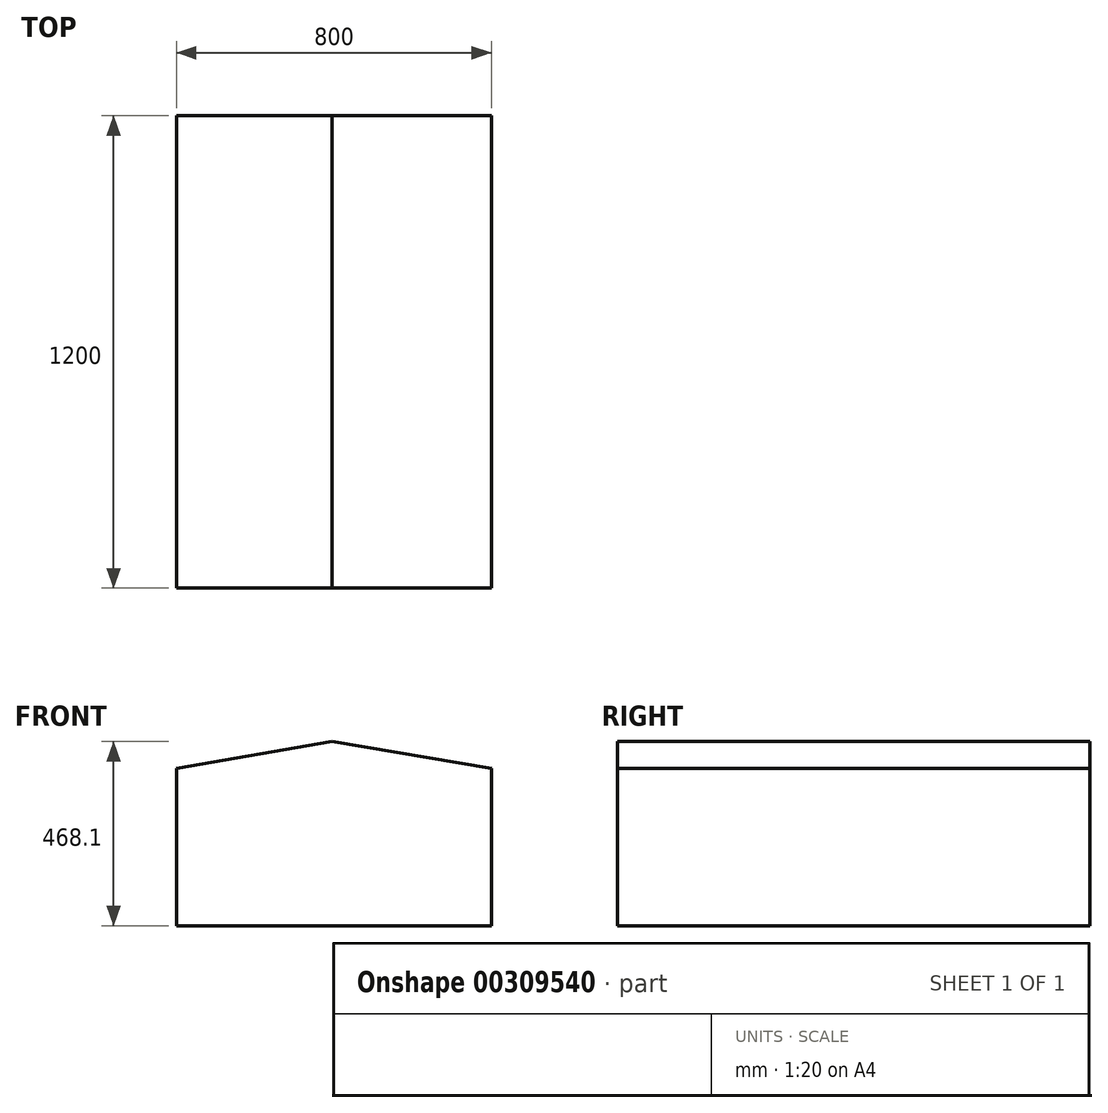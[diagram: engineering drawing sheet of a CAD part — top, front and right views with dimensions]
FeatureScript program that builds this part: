
annotation { "Feature Type Name" : "Feature", "Feature Type Description" : "" }
export const myFeature = defineFeature(function(context is Context, id is Id, definition is map)
    precondition{}
    {
        {
            var Q0;
            Q0=qCreatedBy(makeId("Front.planeOp"),FACE);
            var sketch = newSketch(context, id + "F0", { "sketchPlane" : qUnion([Q0])});
            skLineSegment(sketch, "E0.bottom", {"start": v(-277.48, 197.42) * mm, "end": v(522.52, 197.42) * mm});
            skLineSegment(sketch, "E0.top", {"start": v(-277.48, -202.58) * mm, "end": v(522.52, -202.58) * mm});
            skLineSegment(sketch, "E0.left", {"start": v(-277.48, 197.42) * mm, "end": v(-277.48, -202.58) * mm});
            skLineSegment(sketch, "E0.right", {"start": v(522.52, 197.42) * mm, "end": v(522.52, -202.58) * mm});
            skLineSegment(sketch, "E1", {"start": v(-277.48, 197.42) * mm, "end": v(122.52, 197.42) * mm});
            skLineSegment(sketch, "E2", {"start": v(122.52, 197.42) * mm, "end": v(522.52, 197.42) * mm});
            skLineSegment(sketch, "E3", {"start": v(-277.48, 197.42) * mm, "end": v(117.77, 265.52) * mm});
            skLineSegment(sketch, "E4", {"start": v(522.52, 197.42) * mm, "end": v(117.77, 265.52) * mm});
            skSolve(sketch);
        }
        {
            var Q0;
            Q0 = qSketchRegion(id + "F0", true);
            extrude(context, id + "F1", {"entities" : qUnion([Q0]), "depth" : 1200 * mm});
        }
    });
